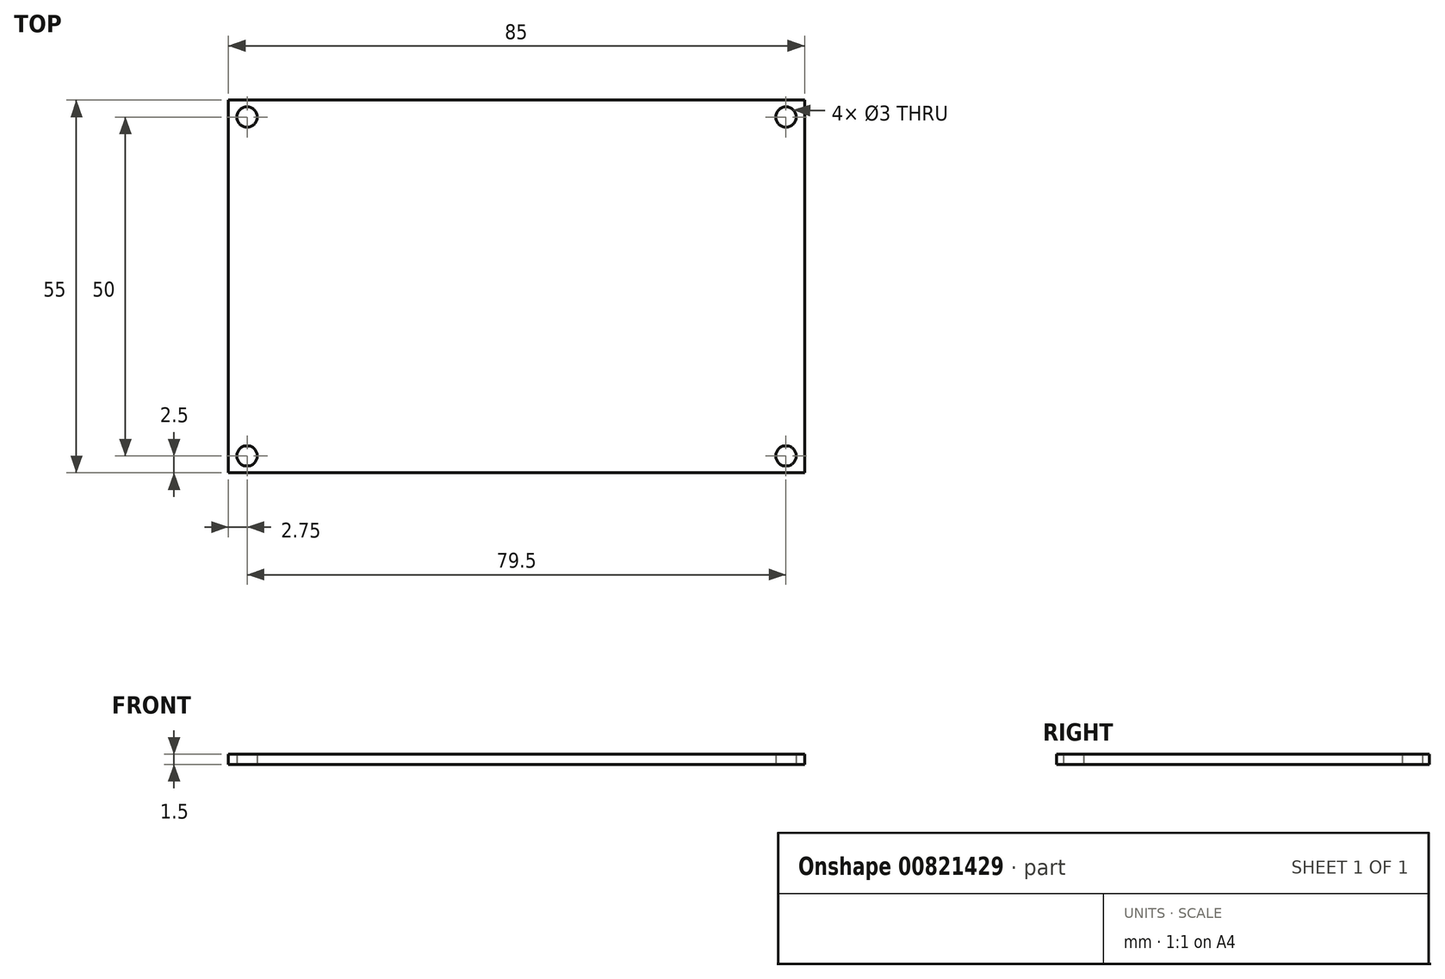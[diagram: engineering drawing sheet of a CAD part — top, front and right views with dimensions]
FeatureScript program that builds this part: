
annotation { "Feature Type Name" : "Feature", "Feature Type Description" : "" }
export const myFeature = defineFeature(function(context is Context, id is Id, definition is map)
    precondition{}
    {
        {
            var Q0;
            Q0=qCreatedBy(makeId("Top.planeOp"),FACE);
            var sketch = newSketch(context, id + "F0", { "sketchPlane" : qUnion([Q0])});
            skLineSegment(sketch, "E0.bottom", {"start": v(42.5, -27.5) * mm, "end": v(-42.5, -27.5) * mm});
            skLineSegment(sketch, "E0.top", {"start": v(42.5, 27.5) * mm, "end": v(-42.5, 27.5) * mm});
            skLineSegment(sketch, "E0.left", {"start": v(42.5, -27.5) * mm, "end": v(42.5, 27.5) * mm});
            skLineSegment(sketch, "E0.right", {"start": v(-42.5, -27.5) * mm, "end": v(-42.5, 27.5) * mm});
            skPoint(sketch, "E0.middle", {"position": v(0, 0) * mm});
            skLineSegment(sketch, "E1.bottom", {"start": v(39.75, -25) * mm, "end": v(-39.75, -25) * mm, "construction": true});
            skLineSegment(sketch, "E1.top", {"start": v(39.75, 25) * mm, "end": v(-39.75, 25) * mm, "construction": true});
            skLineSegment(sketch, "E1.left", {"start": v(39.75, -25) * mm, "end": v(39.75, 25) * mm, "construction": true});
            skLineSegment(sketch, "E1.right", {"start": v(-39.75, -25) * mm, "end": v(-39.75, 25) * mm, "construction": true});
            skCircle(sketch, "E2", {"center": v(39.75, 25) * mm, "radius": 1.5 * mm});
            skCircle(sketch, "E3", {"center": v(39.75, -25) * mm, "radius": 1.5 * mm});
            skCircle(sketch, "E4", {"center": v(-39.75, -25) * mm, "radius": 1.5 * mm});
            skCircle(sketch, "E5", {"center": v(-39.75, 25) * mm, "radius": 1.5 * mm});
            skSolve(sketch);
        }
        {
            var Q0;
            Q0 = qSketchRegion(id + "F0", true);
            extrude(context, id + "F1", {"entities" : qUnion([Q0]), "depth" : 1.5 * mm, "offsetDistance" : 25 * mm});
        }
    });
